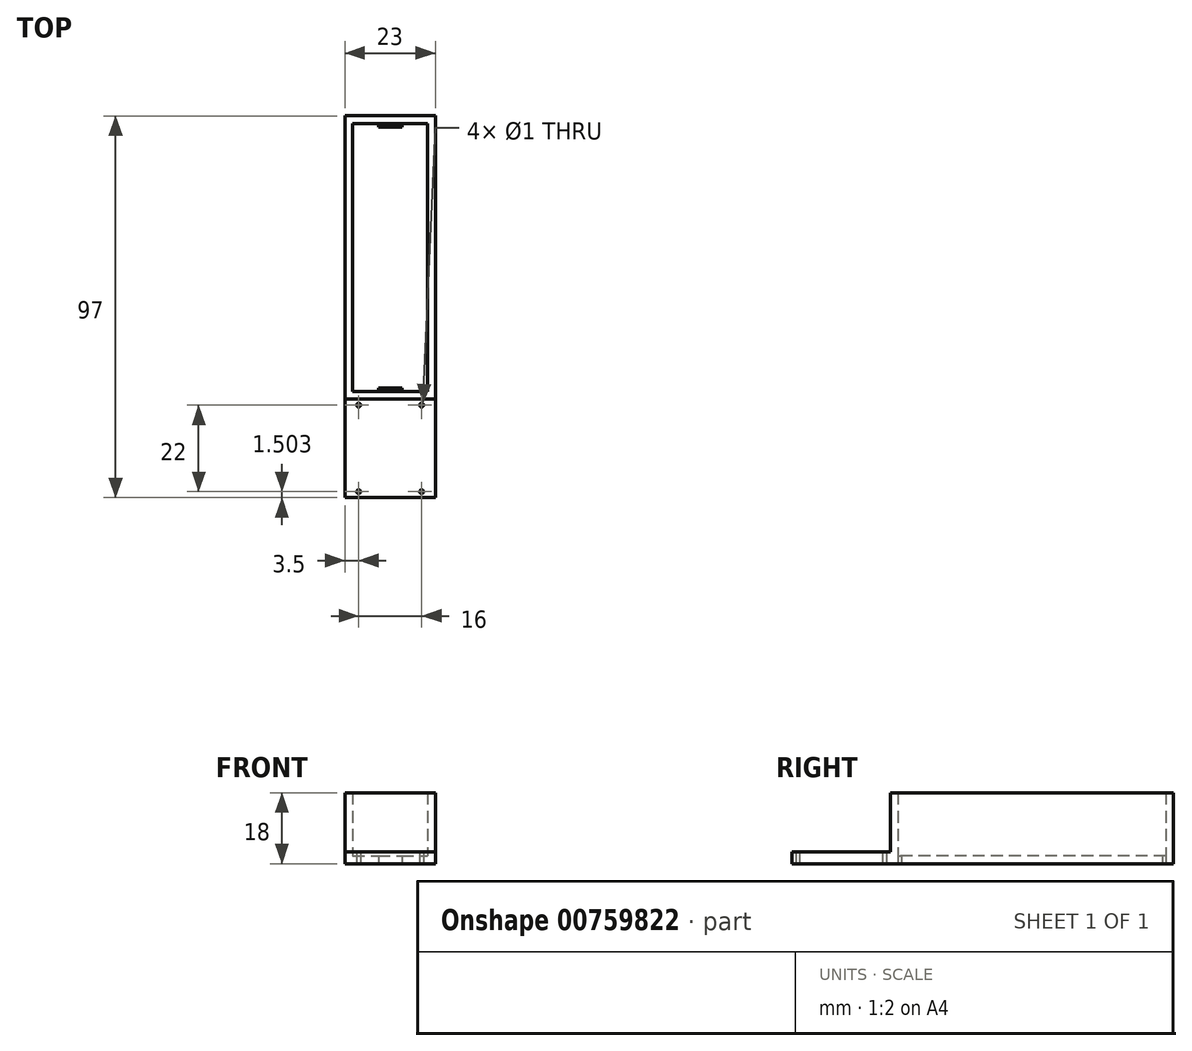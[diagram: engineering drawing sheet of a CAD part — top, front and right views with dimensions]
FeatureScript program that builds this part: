
annotation { "Feature Type Name" : "Feature", "Feature Type Description" : "" }
export const myFeature = defineFeature(function(context is Context, id is Id, definition is map)
    precondition{}
    {
        {
            var Q0;
            Q0=qCreatedBy(makeId("Top.planeOp"),FACE);
            var sketch = newSketch(context, id + "F0", { "sketchPlane" : qUnion([Q0])});
            skLineSegment(sketch, "E0", {"start": v(0, 0) * mm, "end": v(-9.5, 0) * mm, "construction": true});
            skLineSegment(sketch, "E1", {"start": v(0, 54.44) * mm, "end": v(0, -13.56) * mm, "construction": true});
            skLineSegment(sketch, "E2", {"start": v(-9.5, 54.44) * mm, "end": v(0, 54.44) * mm});
            skLineSegment(sketch, "E3", {"start": v(0, -13.56) * mm, "end": v(-9.5, -13.56) * mm});
            skLineSegment(sketch, "E4", {"start": v(-9.5, 54.44) * mm, "end": v(-9.5, -13.56) * mm});
            skLineSegment(sketch, "E5", {"start": v(0, -15.56) * mm, "end": v(-11.5, -15.56) * mm});
            skLineSegment(sketch, "E6", {"start": v(-11.5, -15.56) * mm, "end": v(-11.5, 56.44) * mm});
            skLineSegment(sketch, "E7", {"start": v(-11.5, 56.44) * mm, "end": v(0, 56.44) * mm});
            skLineSegment(sketch, "E8", {"start": v(-11.5, -15.56) * mm, "end": v(-11.5, -40.56) * mm});
            skLineSegment(sketch, "E9", {"start": v(-11.5, -40.56) * mm, "end": v(0, -40.56) * mm});
            skLineSegment(sketch, "E10.MirrorCS", {"start": v(11.5, 56.44) * mm, "end": v(0, 56.44) * mm});
            skLineSegment(sketch, "E11.MirrorCS", {"start": v(9.5, 54.44) * mm, "end": v(0, 54.44) * mm});
            skLineSegment(sketch, "E12.MirrorCS", {"start": v(11.5, -15.56) * mm, "end": v(11.5, 56.44) * mm});
            skLineSegment(sketch, "E13.MirrorCS", {"start": v(9.5, 54.44) * mm, "end": v(9.5, -13.56) * mm});
            skLineSegment(sketch, "E14.MirrorCS", {"start": v(0, -13.56) * mm, "end": v(9.5, -13.56) * mm});
            skLineSegment(sketch, "E15.MirrorCS", {"start": v(0, -15.56) * mm, "end": v(11.5, -15.56) * mm});
            skLineSegment(sketch, "E16.MirrorCS", {"start": v(11.5, -40.56) * mm, "end": v(0, -40.56) * mm});
            skLineSegment(sketch, "E17.MirrorCS", {"start": v(11.5, -15.56) * mm, "end": v(11.5, -40.56) * mm});
            skLineSegment(sketch, "E18", {"start": v(-11.5, -17.06) * mm, "end": v(-8, -17.06) * mm, "construction": true});
            skLineSegment(sketch, "E19", {"start": v(-8, -17.06) * mm, "end": v(-8, -15.56) * mm, "construction": true});
            skCircle(sketch, "E20", {"center": v(-8, -17.06) * mm, "radius": 0.5 * mm});
            skLineSegment(sketch, "E21", {"start": v(8, -15.56) * mm, "end": v(8, -17.06) * mm, "construction": true});
            skLineSegment(sketch, "E22", {"start": v(8, -17.06) * mm, "end": v(11.5, -17.06) * mm, "construction": true});
            skCircle(sketch, "E23", {"center": v(8, -17.06) * mm, "radius": 0.5 * mm});
            skLineSegment(sketch, "E24", {"start": v(-11.5, -39.06) * mm, "end": v(-8, -39.06) * mm, "construction": true});
            skLineSegment(sketch, "E25", {"start": v(-8, -39.06) * mm, "end": v(-8, -40.56) * mm, "construction": true});
            skCircle(sketch, "E26", {"center": v(-8, -39.06) * mm, "radius": 0.5 * mm});
            skLineSegment(sketch, "E27", {"start": v(8, -40.56) * mm, "end": v(8, -39.06) * mm, "construction": true});
            skLineSegment(sketch, "E28", {"start": v(8, -39.06) * mm, "end": v(11.5, -39.06) * mm, "construction": true});
            skCircle(sketch, "E29", {"center": v(8, -39.06) * mm, "radius": 0.5 * mm});
            skLineSegment(sketch, "E30", {"start": v(-3, 54.44) * mm, "end": v(-3, 53.64) * mm});
            skLineSegment(sketch, "E31", {"start": v(-3, 53.64) * mm, "end": v(0, 53.64) * mm});
            skLineSegment(sketch, "E32.MirrorCS", {"start": v(3, 53.64) * mm, "end": v(0, 53.64) * mm});
            skLineSegment(sketch, "E33.MirrorCS", {"start": v(3, 54.44) * mm, "end": v(3, 53.64) * mm});
            skLineSegment(sketch, "E34", {"start": v(-3, -13.56) * mm, "end": v(-3, -12.76) * mm});
            skLineSegment(sketch, "E35", {"start": v(-3, -12.76) * mm, "end": v(0, -12.76) * mm});
            skLineSegment(sketch, "E36.MirrorCS", {"start": v(0, -79.96) * mm, "end": v(0, -11.96) * mm, "construction": true});
            skLineSegment(sketch, "E37.MirrorCS", {"start": v(-3, -11.96) * mm, "end": v(-3, -12.76) * mm});
            skLineSegment(sketch, "E38.MirrorCS", {"start": v(3, -12.76) * mm, "end": v(0, -12.76) * mm});
            skLineSegment(sketch, "E39.MirrorCS", {"start": v(3, -13.56) * mm, "end": v(3, -12.76) * mm});
            skSolve(sketch);
        }
        {
            var Q0;
            {var subQ2=sQuery(id+"F0.wireOp",EDGE,"E4");Q0=makeQuery(id+"F0.imprint","IMPRINT",FACE,{"disambiguationData":[TD([[makeQuery(id+"F0.imprint","IMPRINT",EDGE,{"derivedFrom":subQ2}),1.0]])]});}
            extrude(context, id + "F1", {"entities" : qUnion([Q0]), "depth" : 2 * mm, "offsetDistance" : 25 * mm});
        }
        {
            var Q0;
            Q0=makeQuery(id+"F0.imprint","IMPRINT",FACE,{"disambiguationData":[TD([[makeQuery(id+"F0.imprint","IMPRINT",EDGE,{"derivedFrom":sQuery(id+"F0.wireOp",EDGE,"E2")}),1.0]])]});
            extrude(context, id + "F2", {"entities" : qUnion([Q0]), "operationType" : NewBodyOperationType.ADD, "depth" : 18 * mm, "offsetDistance" : 25 * mm});
        }
        {
            var Q0;
            Q0=makeQuery(id+"F0.imprint","IMPRINT",FACE,{"disambiguationData":[TD([[makeQuery(id+"F0.imprint","IMPRINT",EDGE,{"derivedFrom":sQuery(id+"F0.wireOp",EDGE,"E5")}),1.0]])]});
            extrude(context, id + "F3", {"entities" : qUnion([Q0]), "operationType" : NewBodyOperationType.ADD, "depth" : 3 * mm, "offsetDistance" : 25 * mm});
        }
    });
